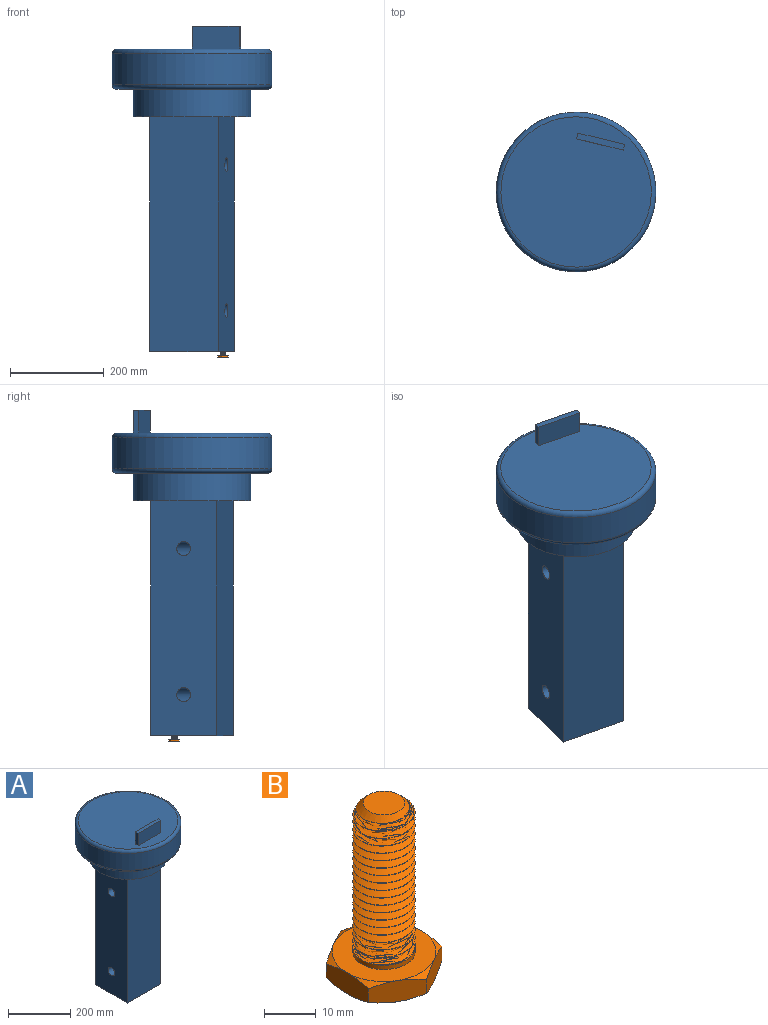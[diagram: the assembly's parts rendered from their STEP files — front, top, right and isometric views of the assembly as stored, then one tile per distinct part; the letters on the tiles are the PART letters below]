
ASSEMBLY  parts=2 mates=1
PART A: 31 faces, bbox 368.2x368.2x693.2 mm
  f0: cylinder r=5.12mm len=49mm, axis (0,0,-1), area 182mm2, adj f20,f27,f28,f29,f30
  f1: plane 150.16x145.16mm, normal (0,0,-1), area 21289.9mm2, adj f3,f4,f5,f6,f21,f23,f25,f27
  f2: plane 320x320mm, normal (0,0,1), area 79136.9mm2, adj f13,f14,f15,f16,f19
  f3: plane 500x145mm, normal (-1,0,0), area 71086.3mm2, adj f1,f5,f6,f8,f11,f12
  f4: plane 500x145mm, normal (1,0,0), area 71086.3mm2, adj f1,f5,f6,f8,f11,f12
  f5: plane 500x150mm, normal (0,-1,0), area 75000mm2, adj f1,f3,f4,f8
  f6: plane 500x150mm, normal (0,1,0), area 75000mm2, adj f1,f3,f4,f8
  f7: cylinder r=125mm len=250mm, axis (0,0,-1), area 45553.1mm2, adj f8,f10
  f8: plane 250x250mm, normal (0,0,-1), area 27337.4mm2, adj f3,f4,f5,f6,f7
  f9: cylinder r=170mm len=340mm, axis (0,0,-1), area 70497.3mm2, adj f18,f19
  f10: plane 320x320mm, normal (0,0,-1), area 31337.4mm2, adj f7,f18
  f11: cylinder r=15mm len=150mm, axis (1,0,0), area 14137.2mm2, adj f3,f4
  f12: cylinder r=15mm len=150mm, axis (1,0,0), area 14137.2mm2, adj f3,f4
  f13: plane 102.39x48mm, normal (0,1,0), area 4914.9mm2, adj f2,f14,f16,f17
  f14: plane 48x12.58mm, normal (-1,0,0), area 603.7mm2, adj f2,f13,f15,f17
  f15: plane 102.39x48mm, normal (0,-1,0), area 4914.9mm2, adj f2,f14,f16,f17
  f16: plane 48x12.58mm, normal (1,0,0), area 603.7mm2, adj f2,f13,f15,f17
  f17: plane 102.39x12.58mm, normal (0,0,1), area 1287.8mm2, adj f13,f14,f15,f16
  f18: torus R=160mm, axis (0,0,1), area 16419.7mm2, adj f9,f10
  f19: torus R=160mm, axis (0,0,1), area 16419.7mm2, adj f2,f9
  f20: plane 10.25x10.25mm, normal (0,0,-1), area 82.5mm2, adj f0
  f21: cylinder r=6mm len=50mm, axis (0,0,-1), area 1885mm2, adj f1,f22
  f22: plane 12x12mm, normal (0,0,-1), area 113.1mm2, adj f21
  f23: cylinder r=6mm len=50mm, axis (0,0,-1), area 1885mm2, adj f1,f24
  f24: plane 12x12mm, normal (0,0,-1), area 113.1mm2, adj f23
  f25: cylinder r=6mm len=50mm, axis (0,0,-1), area 1885mm2, adj f1,f26
  f26: plane 12x12mm, normal (0,0,-1), area 113.1mm2, adj f25
  f27: cone r=5.12mm half-angle=45deg, axis (0,0,-1), area 18.4mm2, adj f0,f1,f28,f29
  f28: bspline ~50.43x15.24mm, area 1765.9mm2, adj f0,f1,f27,f29,f30
  f29: bspline ~50.14x15.24mm, area 1735.3mm2, adj f0,f1,f27,f28,f30
  f30: plane 1.7x1.47mm, normal (0,-1,0), area 1.3mm2, adj f0,f28,f29
PART B: 44 faces, bbox 24.2x24.2x41.4 mm
  f0: cylinder r=6mm len=12mm, axis (0,0,-1), area 41.3mm2, adj f1,f38,f41,f42,f43
  f1: cylinder r=6mm len=12mm, axis (0,0,-1), area 3.8mm2, adj f0,f2,f41,f42
  f2: cylinder r=6mm len=12mm, axis (0,0,-1), area 3.7mm2, adj f1,f3,f41,f42
  f3: cylinder r=6mm len=12mm, axis (0,0,-1), area 3.8mm2, adj f2,f4,f41,f42
  f4: cylinder r=6mm len=12mm, axis (0,0,-1), area 3.8mm2, adj f3,f5,f41,f42
  f5: cylinder r=6mm len=12mm, axis (0,0,-1), area 3.8mm2, adj f4,f6,f41,f42
  f6: cylinder r=6mm len=12mm, axis (0,0,-1), area 3.8mm2, adj f5,f7,f41,f42
  f7: cylinder r=6mm len=12mm, axis (0,0,-1), area 3.8mm2, adj f6,f8,f41,f42
  f8: cylinder r=6mm len=12mm, axis (0,0,-1), area 3.8mm2, adj f7,f9,f41,f42
  f9: cylinder r=6mm len=12mm, axis (0,0,-1), area 3.8mm2, adj f8,f10,f41,f42
  f10: cylinder r=6mm len=12mm, axis (0,0,-1), area 3.8mm2, adj f9,f11,f41,f42
  f11: cylinder r=6mm len=12mm, axis (0,0,-1), area 3.8mm2, adj f10,f12,f41,f42
  f12: cylinder r=6mm len=12mm, axis (0,0,-1), area 3.8mm2, adj f11,f13,f41,f42
  f13: cylinder r=6mm len=12mm, axis (0,0,-1), area 3.8mm2, adj f12,f14,f41,f42
  f14: cylinder r=6mm len=12mm, axis (0,0,-1), area 3.8mm2, adj f13,f15,f41,f42
  f15: cylinder r=6mm len=12mm, axis (0,0,-1), area 3.8mm2, adj f14,f16,f41,f42
  f16: cylinder r=6mm len=12mm, axis (0,0,-1), area 3.8mm2, adj f15,f17,f41,f42
  f17: cylinder r=6mm len=12mm, axis (0,0,-1), area 3.8mm2, adj f16,f18,f41,f42
  f18: cylinder r=6mm len=9.75mm, axis (0,0,-1), area 1.2mm2, adj f17,f40,f41,f42
  f19: plane 10.95x6.72mm, normal (-0.5,-0.87,0), area 50.7mm2, adj f20,f24,f25,f26,f27,f28
  f20: plane 12.5x5.95mm, normal (-1,0,0), area 50.7mm2, adj f19,f21,f26,f28,f29,f30
  f21: plane 10.95x6.72mm, normal (-0.5,0.87,0), area 50.7mm2, adj f20,f22,f29,f30,f31,f32
  f22: plane 10.95x6.72mm, normal (0.5,0.87,0), area 50.7mm2, adj f21,f23,f31,f32,f33,f34
  f23: plane 12.5x5.95mm, normal (1,0,0), area 50.7mm2, adj f22,f24,f33,f34,f35,f36
  f24: plane 10.95x6.72mm, normal (0.5,-0.87,0), area 50.7mm2, adj f19,f23,f25,f27,f35,f36
  f25: cone r=14.33mm half-angle=60deg, axis (0,0,1), area 9.8mm2, adj f19,f24,f37
  f26: cone r=14.33mm half-angle=60deg, axis (0,0,1), area 9.8mm2, adj f19,f20,f37
  f27: cone r=14.33mm half-angle=60deg, axis (0,0,-1), area 9.8mm2, adj f19,f24,f38
  f28: cone r=14.33mm half-angle=60deg, axis (0,0,-1), area 9.8mm2, adj f19,f20,f38
  f29: cone r=14.33mm half-angle=60deg, axis (0,0,1), area 9.8mm2, adj f20,f21,f37
  f30: cone r=14.33mm half-angle=60deg, axis (0,0,-1), area 9.8mm2, adj f20,f21,f38
  f31: cone r=14.33mm half-angle=60deg, axis (0,0,1), area 9.8mm2, adj f21,f22,f37
  f32: cone r=14.33mm half-angle=60deg, axis (0,0,-1), area 9.8mm2, adj f21,f22,f38
  f33: cone r=14.33mm half-angle=60deg, axis (0,0,1), area 9.8mm2, adj f22,f23,f37
  f34: cone r=14.33mm half-angle=60deg, axis (0,0,-1), area 9.8mm2, adj f22,f23,f38
  f35: cone r=14.33mm half-angle=60deg, axis (0,0,1), area 9.8mm2, adj f23,f24,f37
  f36: cone r=14.33mm half-angle=60deg, axis (0,0,-1), area 9.8mm2, adj f23,f24,f38
  f37: plane 20x20mm, normal (0,0,-1), area 314.2mm2, adj f25,f26,f29,f31,f33,f35
  f38: plane 20x20mm, normal (0,0,1), area 201.1mm2, adj f0,f27,f28,f30,f32,f34,f36
  f39: plane 8x8mm, normal (0,0,1), area 50.3mm2, adj f40
  f40: cone r=4mm half-angle=45deg, axis (0,0,-1), area 55.9mm2, adj f18,f39,f41,f42
  f41: bspline ~35.24x13.86mm, area 1051.7mm2, adj f0,f1,f2,f3,f4,f5,f6,f7
  f42: bspline ~34.37x13.86mm, area 979.5mm2, adj f0,f1,f2,f3,f4,f5,f6,f7
  f43: plane 13.14x13.14mm, normal (0,0,1), area 23.4mm2, adj f0,f41,f42
PLACE A rot(axis=(0,0,1),166.3deg) t=(-402.53,-166.75,-36.46)mm fixed
PLACE B rot(axis=(0,0,-1),132.4deg) t=(-324.36,-57.16,-140.49)mm
MATE cylindrical B.f0 <-> A.f0  axis (0,0,1) through (-324.36,-57.16,-100.49)mm
